# Revit family: SLIMFILTER-600600_KF51560
name_source: partatom
category: Aparatos eléctricos
revit_build: Autodesk Revit 2016 (Build: 20150220_1215(x64)
units: mm (PartAtom-declared; Revit-internal decimal feet)

## family parameters
Compartido = No
Corte con vacíos al cargar = No
Cota de conector redondo = Diámetro de uso
Mantener orientación de anotación = No
Número OmniClass = 23.80.00.00
Punto de cálculo de habitación = No
Se basa en plano de trabajo = No
Siempre vertical = Sí
Tipo de pieza = Caja de conexiones
Título OmniClass = Electric Power and Lighting

## types (1)
- 600600
    Costo = 0 $
    Cumple ErP 2009/125/CE = Si
    Código de montaje = KF51560
    Descripción = UNIDADES DE FILTRACIÓN
    Dimensiones = 695 x 692 x 632 mm
    Fabricante = SALVADOR ESCODA
    Imagen de tipo = slimfilter.jpg
    Intensidad = 2,7A
    Modelo = SLIMFILTER 600600
    Nivel presión sonora = 64 dBa
    Nª Polos = 4
    Potencia = 350W
    URL = www.salvadorescoda.com
    Velocidad = 1352 rpm
    Ventilador = 9/9
